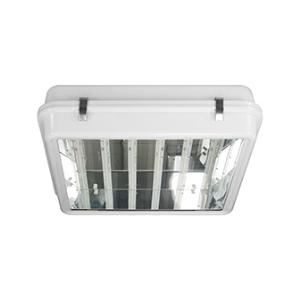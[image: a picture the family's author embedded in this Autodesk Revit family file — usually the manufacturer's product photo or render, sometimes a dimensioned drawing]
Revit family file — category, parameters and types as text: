
# Revit family: 3f_filippi_-_3f_cub_vt_3f_filippi_-_56335_-_3f_cub_led_150w_dali_cr_vt
name_source: partatom
category: Lighting Fixtures
units: mm (PartAtom-declared; Revit-internal decimal feet)

## family parameters
Cut with Voids When Loaded = No
Host = Face
Light Source = No
Part Type = Normal
Room Calculation Point = No
Round Connector Dimension = Use Diameter
Shared = No

## types (1)
- 3F Filippi - 3F Cub VT (1 x LED, 22588 lm, 159 W, 4000 K)
    Apparent Load = 159 VA
    Approval mark = CE
    CIE Flux Codes = 53 86 98 100 100
    Color Rendering = 80
    Color Temperature = 4000 K
    Control Gear = Electronic transformer
    Default Elevation = 1800 mm
    Description = ILLUMINOTECHNICAL
Luminous efficiency 100% (DLOR 100%, ULOR 0%).
Initial luminous flux of the luminaire 22588 lm.
Symmetric wide direct distribution.
Installation Interdistance Transv.D = 1.05 x hu - Long.D = 1.24 x hu.
Tabular UGR (CIE 117 - 4H-8H; S=0.25H; 70/50/20): RUG 24.5 - 26.3.
Beam angle: 94° - 108°.
Luminous efficacy 142 lm/W.
Lifetime (L90/B10): 30000 h. (tq+25°C)
Lifetime (L85/B10): 50000 h. (tq+25°C)
Lifetime (L80/B20): 80000 h. (tq+25°C)
Lifetime (L70/B20): 100000 h. (tq+25°C)
Lifetime (L70/B10): 50000 h. (tq+40°C)
Sudden decreased luminous flux after 50000 hours: 0% (C0).
Photobiological safety in compliance with IEC/TR 62778: RG0 risk exempt, (IEC 62471).
In compliance with IEC/EN 62722-2-1 - IEC/EN 62717 standards.

SOURCE
6 linear LED modules 25W/840.
Energy efficiency class (UE 2019/2020 - UE 2019/2015): C.
CIE 13.3 Colour rendering index: CRI >80 (R9 <50%).
IES TM-30 Fidelity Index: Rf = 84 Rg = 95.
CCT nominal colour temperature 4000 K.
Colour initial tolerance (MacAdam): SDCM 3.

MECHANICAL
Housing with double casing in pressed aluminium, powder-coated in white epoxy-polyester, hinged opening.
Quick connection in polycarbonate M20x1.5 cable gland for access to the terminal block.
Ecologic anti-aging injected sealing gasket.
Stainless steel clips.
Total flow recuperator in specular aluminium, with superficial titanium-magnesium treatment, non-iridescent.
Transparent, non-combustible tempered glass.
Fixing bracket for busbar or suspension in galvanised steel.
Luminaire with limited surface temperature. - D - (EN 60598-2-24)
Dimensions: 680x680 mm, height 187 mm. Weight 11.52 kg.
IP64 protection degree.
Mechanical strength to impacts IK10 (20 joule).
Glow-wire test resistance 960°C.

ELECTRICAL
Halogen Free DALI-2, PUSH-DIM, electronic wiring 230V-50/60Hz, power factor 0.95 at full load, THD <25%, constant output current, class I, 2 driver, 2 DALI addresses.
Power of the luminaire 159 W.
ENEC - CE.
SAFE FLICKER: PstLM=<1 and SVM=<0.4 (IEC TR 61547-1 and IEC TR 63158), to ensure a more comfortable and safe light.
Luminaire compliant with EN 60598-2-22 for power supply from a centralised emergency system CPSS (Central Power Supply System), not incorporated in the luminaire - high risk areas excluded. The default power and flux are 100% in AC and 15% in DC.
Ambient temperature from -20°C to +40°C.
Temperature class T6 max 85°C.
Quick connection.
Relative humidity UR: <85%.

INSTALLATION
Ceiling / Suspended.
All accessories dedicated to this product are available on the Catalog and on our website www.3F-Filippi.com.

APPLICATIONS
Areas with high ceilings, industrial/warehouses and open areas.

LIGHT MANAGEMENT
Recommended minimum setting: 10%.
The device, equipped with DALI-2 driver, can be controlled manually with 3F Easy Dim technology or automatically/manually with 3F Smart Dimming technology and/or centralised DALI systems.
DALI-2 certification guarantees interoperability with other devices with the same certification.
In electrical systems without a regulation system (manual or automatic) and DALI bus, a suitable jumper must be made on the DA-DA terminals of the appliance.

WARNING
Fixture not suitable for cold stores with an ambient temperature <0°C and/or relative humidity >85%.
Luminaire designed for disposal/recycling at end-of-life.
Replaceable (LED only) light source by a professional. Replaceable control gear by a professional.
    Height = 187 mm
    Lamp = 1 x LED
    Lamp Light Flux = 22588 lm
    Lamp Power = 159 W
    Lamp count = 1
    Length = 680 mm
    Lifetime = 50000 h
    Luminous efficacy = 142 lm/W
    Manufacturer = 3F Filippi
    ModVariant = No
    Model = 3F Filippi - 56335 - 3F CUB LED 150W DALI CR VT
    Mounting Place = Ceiling
    Mounting Type = Pendant
    Number of Poles = 1
    OnlyDefault = Yes
    Power Factor = 1
    Product Name = 3F Filippi - 3F Cub VT
    Product group = pendant luminaire
    ProductGroupID = 9
    Protection Class = Protection class I
    Protection Degree = IP 64
    RLX_Detail_Level = 1
    RLX_Emergency_Light_Flux = 0 lm
    RLX_Emergency_Type = 0
    RLX_Emergency_Type_DB = No
    RlxData = <blob elided: 51737 chars, md5=ae96c1d0>
    Socket = socket
    Standby Power = 0 W
    System Light Flux = 22588 lm
    System Power = 159 W
    Type Comments = Product without accessories
    Type Image = 3ffilippi_56335.jpg
    URL = http://relux.com
    VarID = ---
    Voltage = 0 V
    Weight = 0.00 kg
    Width = 680 mm

## geometry (parser evidence)
native form markers: Blend x4, Sweep x11
no freeform markers — native parametric forms only
